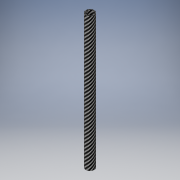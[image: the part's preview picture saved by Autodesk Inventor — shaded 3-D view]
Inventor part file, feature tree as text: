
AUTODESK INVENTOR PART (.ipt)
format: ipt  version: 2018 (Build 220112000, 112)  size: 98,816 bytes
history: native  units: in
note: dims shown in document units (in); Inventor stores cm internally (conversion verified against a paired STEP export)
features: extrude x1, sketch x1
ambient origin geometry x8: Origin, YZ Plane, XZ Plane, XY Plane, X Axis, Y Axis, Z Axis, Center Point
bodies: Solid1 (feature_tree)
feature tree (2):
  extrude  "Extrusion1"  Depth=5.9896in
  sketch  "Sketch1"  dims[d0=0.375in d1=0.31in d2=5.9896in d3=0.0in]
